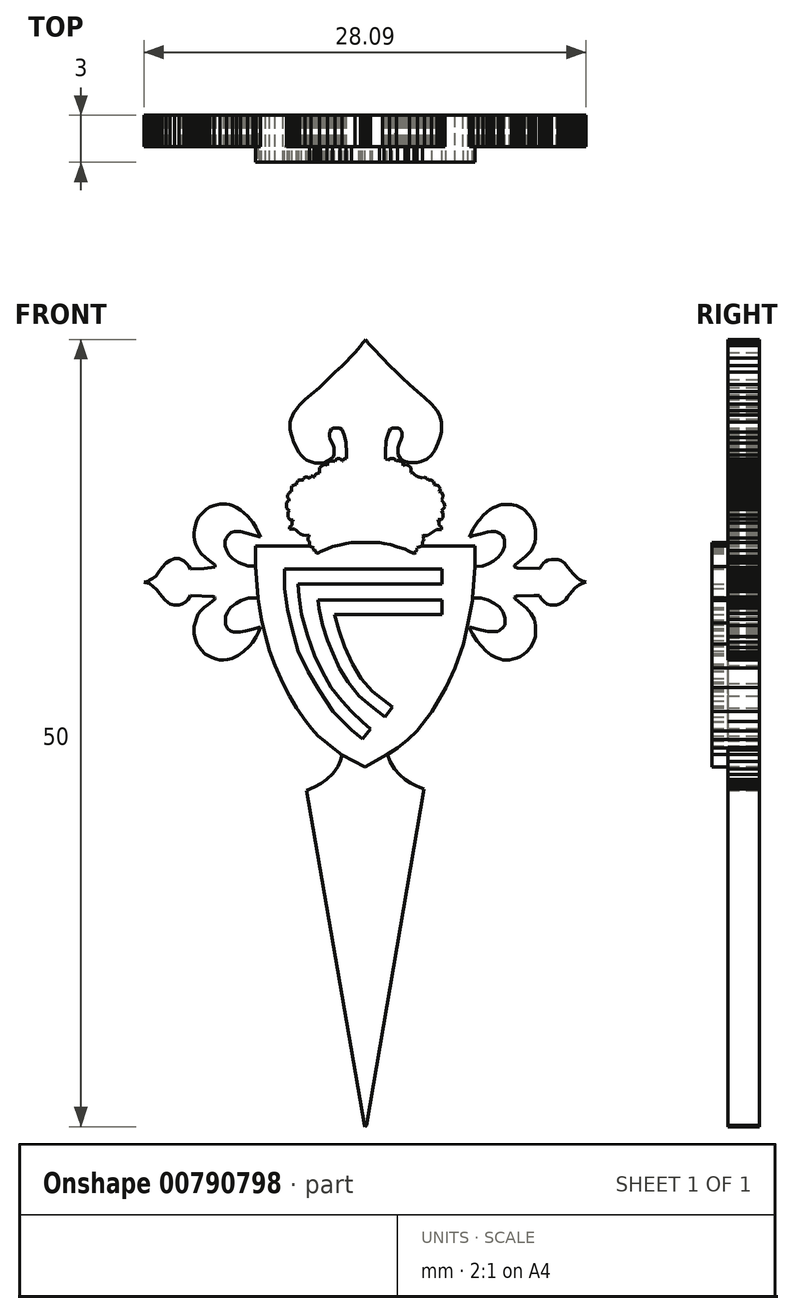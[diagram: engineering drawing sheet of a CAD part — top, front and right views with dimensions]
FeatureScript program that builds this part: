
annotation { "Feature Type Name" : "Feature", "Feature Type Description" : "" }
export const myFeature = defineFeature(function(context is Context, id is Id, definition is map)
    precondition{}
    {
        {
            var Q0;
            Q0=qCreatedBy(makeId("Front.planeOp"),FACE);
            var sketch = newSketch(context, id + "F0", { "sketchPlane" : qUnion([Q0])});
            skLineSegment(sketch, "E0", {"start": v(14.06, 0) * mm, "end": v(10.39, 21.27) * mm});
            skPoint(sketch, "E0.startSnap0", {"position": v(14.06, -0.08) * mm});
            skLineSegment(sketch, "E1", {"start": v(10.39, 21.27) * mm, "end": v(10.9, 21.5) * mm});
            skLineSegment(sketch, "E2", {"start": v(10.9, 21.5) * mm, "end": v(11.32, 21.71) * mm});
            skLineSegment(sketch, "E3", {"start": v(11.32, 21.71) * mm, "end": v(11.67, 21.99) * mm});
            skLineSegment(sketch, "E4", {"start": v(11.67, 21.99) * mm, "end": v(12.06, 22.35) * mm});
            skLineSegment(sketch, "E5", {"start": v(12.06, 22.35) * mm, "end": v(12.39, 22.8) * mm});
            skLineSegment(sketch, "E6", {"start": v(12.39, 22.8) * mm, "end": v(12.57, 23.17) * mm});
            skLineSegment(sketch, "E7", {"start": v(12.57, 23.17) * mm, "end": v(12.65, 23.55) * mm});
            skLineSegment(sketch, "E8", {"start": v(12.65, 23.55) * mm, "end": v(11.92, 24.1) * mm});
            skLineSegment(sketch, "E9", {"start": v(11.92, 24.1) * mm, "end": v(11.54, 24.4) * mm});
            skLineSegment(sketch, "E10", {"start": v(11.54, 24.4) * mm, "end": v(11.15, 24.74) * mm});
            skLineSegment(sketch, "E11", {"start": v(11.15, 24.74) * mm, "end": v(10.71, 25.21) * mm});
            skLineSegment(sketch, "E12", {"start": v(10.71, 25.21) * mm, "end": v(10.37, 25.64) * mm});
            skLineSegment(sketch, "E13", {"start": v(10.37, 25.64) * mm, "end": v(9.75, 26.5) * mm});
            skLineSegment(sketch, "E14", {"start": v(9.75, 26.5) * mm, "end": v(9.3, 27.27) * mm});
            skLineSegment(sketch, "E15", {"start": v(9.3, 27.27) * mm, "end": v(8.9, 28.06) * mm});
            skLineSegment(sketch, "E16", {"start": v(8.9, 28.06) * mm, "end": v(8.4, 29.21) * mm});
            skLineSegment(sketch, "E17", {"start": v(8.4, 29.21) * mm, "end": v(8.05, 30.15) * mm});
            skLineSegment(sketch, "E18", {"start": v(8.05, 30.15) * mm, "end": v(7.79, 31.09) * mm});
            skLineSegment(sketch, "E19", {"start": v(7.79, 31.09) * mm, "end": v(7.54, 32.09) * mm});
            skLineSegment(sketch, "E20", {"start": v(7.54, 32.09) * mm, "end": v(7.4, 32.9) * mm});
            skLineSegment(sketch, "E21", {"start": v(7.4, 32.9) * mm, "end": v(7.32, 33.46) * mm});
            skLineSegment(sketch, "E22", {"start": v(7.32, 33.46) * mm, "end": v(7.32, 33.5) * mm});
            skLineSegment(sketch, "E23", {"start": v(6.97, 33.5) * mm, "end": v(6.72, 33.5) * mm});
            skLineSegment(sketch, "E24", {"start": v(6.72, 33.5) * mm, "end": v(6.45, 33.4) * mm});
            skLineSegment(sketch, "E25", {"start": v(6.45, 33.4) * mm, "end": v(6.24, 33.33) * mm});
            skLineSegment(sketch, "E26", {"start": v(6.24, 33.33) * mm, "end": v(5.92, 33.16) * mm});
            skLineSegment(sketch, "E27", {"start": v(5.92, 33.16) * mm, "end": v(5.56, 32.88) * mm});
            skLineSegment(sketch, "E28", {"start": v(5.56, 32.88) * mm, "end": v(5.37, 32.61) * mm});
            skLineSegment(sketch, "E29", {"start": v(5.37, 32.61) * mm, "end": v(5.26, 32.32) * mm});
            skLineSegment(sketch, "E30", {"start": v(5.26, 32.32) * mm, "end": v(5.26, 31.8) * mm});
            skLineSegment(sketch, "E31", {"start": v(5.26, 31.8) * mm, "end": v(5.39, 31.56) * mm});
            skLineSegment(sketch, "E32", {"start": v(5.39, 31.56) * mm, "end": v(5.58, 31.4) * mm});
            skLineSegment(sketch, "E33", {"start": v(5.58, 31.4) * mm, "end": v(5.77, 31.33) * mm});
            skLineSegment(sketch, "E34", {"start": v(5.77, 31.33) * mm, "end": v(6.17, 31.33) * mm});
            skLineSegment(sketch, "E35", {"start": v(6.17, 31.33) * mm, "end": v(6.53, 31.4) * mm});
            skLineSegment(sketch, "E36", {"start": v(6.53, 31.4) * mm, "end": v(6.9, 31.49) * mm});
            skLineSegment(sketch, "E37", {"start": v(6.9, 31.49) * mm, "end": v(7.47, 31.64) * mm});
            skLineSegment(sketch, "E38", {"start": v(7.47, 31.64) * mm, "end": v(7.36, 31.33) * mm});
            skLineSegment(sketch, "E39", {"start": v(7.36, 31.33) * mm, "end": v(7.18, 31.03) * mm});
            skLineSegment(sketch, "E40", {"start": v(7.18, 31.03) * mm, "end": v(6.97, 30.68) * mm});
            skLineSegment(sketch, "E41", {"start": v(6.97, 30.68) * mm, "end": v(6.76, 30.46) * mm});
            skLineSegment(sketch, "E42", {"start": v(6.76, 30.46) * mm, "end": v(6.38, 30.1) * mm});
            skLineSegment(sketch, "E43", {"start": v(6.38, 30.1) * mm, "end": v(6.03, 29.84) * mm});
            skLineSegment(sketch, "E44", {"start": v(6.03, 29.84) * mm, "end": v(5.67, 29.65) * mm});
            skLineSegment(sketch, "E45", {"start": v(5.67, 29.65) * mm, "end": v(5.37, 29.6) * mm});
            skLineSegment(sketch, "E46", {"start": v(5.37, 29.6) * mm, "end": v(5.12, 29.56) * mm});
            skLineSegment(sketch, "E47", {"start": v(5.12, 29.56) * mm, "end": v(4.88, 29.56) * mm});
            skLineSegment(sketch, "E48", {"start": v(4.88, 29.56) * mm, "end": v(4.65, 29.63) * mm});
            skLineSegment(sketch, "E49", {"start": v(4.65, 29.63) * mm, "end": v(4.4, 29.72) * mm});
            skLineSegment(sketch, "E50", {"start": v(4.4, 29.72) * mm, "end": v(3.96, 29.96) * mm});
            skLineSegment(sketch, "E51", {"start": v(3.96, 29.96) * mm, "end": v(3.7, 30.22) * mm});
            skLineSegment(sketch, "E52", {"start": v(3.7, 30.22) * mm, "end": v(3.45, 30.57) * mm});
            skLineSegment(sketch, "E53", {"start": v(3.45, 30.57) * mm, "end": v(3.3, 30.96) * mm});
            skLineSegment(sketch, "E54", {"start": v(3.3, 30.96) * mm, "end": v(3.24, 31.25) * mm});
            skLineSegment(sketch, "E55", {"start": v(3.24, 31.25) * mm, "end": v(3.24, 31.7) * mm});
            skLineSegment(sketch, "E56", {"start": v(3.51, 32.48) * mm, "end": v(3.7, 32.7) * mm});
            skLineSegment(sketch, "E57", {"start": v(3.7, 32.7) * mm, "end": v(3.89, 32.89) * mm});
            skLineSegment(sketch, "E58", {"start": v(3.89, 32.89) * mm, "end": v(4.12, 33.07) * mm});
            skLineSegment(sketch, "E59", {"start": v(4.12, 33.07) * mm, "end": v(4.55, 33.4) * mm});
            skLineSegment(sketch, "E60", {"start": v(4.55, 33.4) * mm, "end": v(4.58, 33.5) * mm});
            skLineSegment(sketch, "E61", {"start": v(4.58, 33.5) * mm, "end": v(4.55, 33.57) * mm});
            skLineSegment(sketch, "E62", {"start": v(4.55, 33.57) * mm, "end": v(4.45, 33.6) * mm});
            skLineSegment(sketch, "E63", {"start": v(4.45, 33.6) * mm, "end": v(3.02, 33.66) * mm});
            skLineSegment(sketch, "E64", {"start": v(3.02, 33.66) * mm, "end": v(2.88, 33.4) * mm});
            skLineSegment(sketch, "E65", {"start": v(2.88, 33.4) * mm, "end": v(2.7, 33.25) * mm});
            skLineSegment(sketch, "E66", {"start": v(2.7, 33.25) * mm, "end": v(2.47, 33.13) * mm});
            skLineSegment(sketch, "E67", {"start": v(2.47, 33.13) * mm, "end": v(2.3, 33.07) * mm});
            skLineSegment(sketch, "E68", {"start": v(2.3, 33.07) * mm, "end": v(1.97, 33.07) * mm});
            skLineSegment(sketch, "E69", {"start": v(1.97, 33.07) * mm, "end": v(1.73, 33.12) * mm});
            skLineSegment(sketch, "E70", {"start": v(1.73, 33.12) * mm, "end": v(1.59, 33.23) * mm});
            skLineSegment(sketch, "E71", {"start": v(1.59, 33.23) * mm, "end": v(1.39, 33.4) * mm});
            skLineSegment(sketch, "E72", {"start": v(1.39, 33.4) * mm, "end": v(1.1, 33.76) * mm});
            skLineSegment(sketch, "E73", {"start": v(1.1, 33.76) * mm, "end": v(0.87, 34.05) * mm});
            skLineSegment(sketch, "E74", {"start": v(0.87, 34.05) * mm, "end": v(0.66, 34.23) * mm});
            skLineSegment(sketch, "E75", {"start": v(0.66, 34.23) * mm, "end": v(0.41, 34.4) * mm});
            skLineSegment(sketch, "E76", {"start": v(0.41, 34.4) * mm, "end": v(0.14, 34.49) * mm});
            skLineSegment(sketch, "E77", {"start": v(0.14, 34.49) * mm, "end": v(0.06, 34.5) * mm});
            skLineSegment(sketch, "E78", {"start": v(0.06, 34.5) * mm, "end": v(0.14, 34.52) * mm});
            skLineSegment(sketch, "E79", {"start": v(0.14, 34.52) * mm, "end": v(0.25, 34.55) * mm});
            skLineSegment(sketch, "E80", {"start": v(0.25, 34.55) * mm, "end": v(0.35, 34.59) * mm});
            skLineSegment(sketch, "E81", {"start": v(0.35, 34.59) * mm, "end": v(0.43, 34.64) * mm});
            skLineSegment(sketch, "E82", {"start": v(0.43, 34.64) * mm, "end": v(0.62, 34.74) * mm});
            skLineSegment(sketch, "E83", {"start": v(0.62, 34.74) * mm, "end": v(0.82, 34.91) * mm});
            skLineSegment(sketch, "E84", {"start": v(0.82, 34.91) * mm, "end": v(1.02, 35.17) * mm});
            skLineSegment(sketch, "E85", {"start": v(1.02, 35.17) * mm, "end": v(1.22, 35.44) * mm});
            skLineSegment(sketch, "E86", {"start": v(1.22, 35.44) * mm, "end": v(1.46, 35.7) * mm});
            skLineSegment(sketch, "E87", {"start": v(1.46, 35.7) * mm, "end": v(1.72, 35.9) * mm});
            skLineSegment(sketch, "E88", {"start": v(1.72, 35.9) * mm, "end": v(2, 36) * mm});
            skLineSegment(sketch, "E89", {"start": v(2, 36) * mm, "end": v(2.3, 36) * mm});
            skLineSegment(sketch, "E90", {"start": v(2.3, 36) * mm, "end": v(2.6, 35.84) * mm});
            skLineSegment(sketch, "E91", {"start": v(2.6, 35.84) * mm, "end": v(2.8, 35.67) * mm});
            skLineSegment(sketch, "E92", {"start": v(2.8, 35.67) * mm, "end": v(2.93, 35.5) * mm});
            skLineSegment(sketch, "E93", {"start": v(2.93, 35.5) * mm, "end": v(3.02, 35.35) * mm});
            skLineSegment(sketch, "E94", {"start": v(3.02, 35.35) * mm, "end": v(3.89, 35.39) * mm});
            skLineSegment(sketch, "E95", {"start": v(3.89, 35.39) * mm, "end": v(4.58, 35.46) * mm});
            skLineSegment(sketch, "E96", {"start": v(4.58, 35.46) * mm, "end": v(4.58, 35.56) * mm});
            skLineSegment(sketch, "E97", {"start": v(4.58, 35.56) * mm, "end": v(4.55, 35.62) * mm});
            skLineSegment(sketch, "E98", {"start": v(4.55, 35.62) * mm, "end": v(4.3, 35.8) * mm});
            skLineSegment(sketch, "E99", {"start": v(4.3, 35.8) * mm, "end": v(3.97, 36.09) * mm});
            skLineSegment(sketch, "E100", {"start": v(3.97, 36.09) * mm, "end": v(3.7, 36.33) * mm});
            skLineSegment(sketch, "E101", {"start": v(3.7, 36.33) * mm, "end": v(3.5, 36.6) * mm});
            skLineSegment(sketch, "E102", {"start": v(3.5, 36.6) * mm, "end": v(3.35, 36.91) * mm});
            skLineSegment(sketch, "E103", {"start": v(3.35, 36.91) * mm, "end": v(3.28, 37.17) * mm});
            skLineSegment(sketch, "E104", {"start": v(3.28, 37.17) * mm, "end": v(3.23, 37.4) * mm});
            skLineSegment(sketch, "E105", {"start": v(3.23, 37.4) * mm, "end": v(3.23, 37.58) * mm});
            skLineSegment(sketch, "E106", {"start": v(3.23, 37.58) * mm, "end": v(3.28, 37.88) * mm});
            skLineSegment(sketch, "E107", {"start": v(3.28, 37.88) * mm, "end": v(3.34, 38.12) * mm});
            skLineSegment(sketch, "E108", {"start": v(3.34, 38.12) * mm, "end": v(3.42, 38.4) * mm});
            skLineSegment(sketch, "E109", {"start": v(3.42, 38.4) * mm, "end": v(3.57, 38.67) * mm});
            skLineSegment(sketch, "E110", {"start": v(3.57, 38.67) * mm, "end": v(3.78, 38.9) * mm});
            skLineSegment(sketch, "E111", {"start": v(3.78, 38.9) * mm, "end": v(4.02, 39.12) * mm});
            skLineSegment(sketch, "E112", {"start": v(4.02, 39.12) * mm, "end": v(4.25, 39.27) * mm});
            skLineSegment(sketch, "E113", {"start": v(4.25, 39.27) * mm, "end": v(4.52, 39.38) * mm});
            skLineSegment(sketch, "E114", {"start": v(4.91, 39.48) * mm, "end": v(5.32, 39.48) * mm});
            skLineSegment(sketch, "E115", {"start": v(5.32, 39.48) * mm, "end": v(5.5, 39.43) * mm});
            skLineSegment(sketch, "E116", {"start": v(5.5, 39.43) * mm, "end": v(5.7, 39.36) * mm});
            skLineSegment(sketch, "E117", {"start": v(5.7, 39.36) * mm, "end": v(5.94, 39.25) * mm});
            skLineSegment(sketch, "E118", {"start": v(5.94, 39.25) * mm, "end": v(6.2, 39.1) * mm});
            skLineSegment(sketch, "E119", {"start": v(6.66, 38.7) * mm, "end": v(7, 38.3) * mm});
            skLineSegment(sketch, "E120", {"start": v(7, 38.3) * mm, "end": v(7.19, 37.98) * mm});
            skLineSegment(sketch, "E121", {"start": v(7.19, 37.98) * mm, "end": v(7.48, 37.38) * mm});
            skLineSegment(sketch, "E122", {"start": v(7.48, 37.38) * mm, "end": v(6.43, 37.67) * mm});
            skLineSegment(sketch, "E123", {"start": v(6.43, 37.67) * mm, "end": v(6.22, 37.73) * mm});
            skLineSegment(sketch, "E124", {"start": v(6.22, 37.73) * mm, "end": v(5.83, 37.73) * mm});
            skLineSegment(sketch, "E125", {"start": v(5.83, 37.73) * mm, "end": v(5.6, 37.67) * mm});
            skLineSegment(sketch, "E126", {"start": v(5.6, 37.67) * mm, "end": v(5.4, 37.48) * mm});
            skLineSegment(sketch, "E127", {"start": v(5.4, 37.48) * mm, "end": v(5.27, 37.27) * mm});
            skLineSegment(sketch, "E128", {"start": v(5.27, 37.27) * mm, "end": v(5.23, 37.12) * mm});
            skLineSegment(sketch, "E129", {"start": v(5.23, 37.12) * mm, "end": v(5.23, 36.8) * mm});
            skLineSegment(sketch, "E130", {"start": v(5.23, 36.8) * mm, "end": v(5.31, 36.55) * mm});
            skLineSegment(sketch, "E131", {"start": v(5.31, 36.55) * mm, "end": v(5.48, 36.23) * mm});
            skLineSegment(sketch, "E132", {"start": v(5.48, 36.23) * mm, "end": v(5.7, 36) * mm});
            skLineSegment(sketch, "E133", {"start": v(5.7, 36) * mm, "end": v(6.08, 35.75) * mm});
            skLineSegment(sketch, "E134", {"start": v(6.08, 35.75) * mm, "end": v(6.67, 35.52) * mm});
            skLineSegment(sketch, "E135", {"start": v(6.67, 35.52) * mm, "end": v(7.16, 35.52) * mm});
            skLineSegment(sketch, "E136", {"start": v(7.16, 35.52) * mm, "end": v(7.16, 36.8) * mm});
            skLineSegment(sketch, "E137", {"start": v(10.58, 36.8) * mm, "end": v(10.58, 37.07) * mm});
            skLineSegment(sketch, "E138", {"start": v(10.58, 37.07) * mm, "end": v(10.48, 37.16) * mm});
            skLineSegment(sketch, "E139", {"start": v(10.48, 37.16) * mm, "end": v(10.48, 37.34) * mm});
            skLineSegment(sketch, "E140", {"start": v(10.48, 37.34) * mm, "end": v(10.54, 37.4) * mm});
            skLineSegment(sketch, "E141", {"start": v(10.54, 37.4) * mm, "end": v(10.54, 37.5) * mm});
            skLineSegment(sketch, "E142", {"start": v(10.54, 37.5) * mm, "end": v(10.35, 37.47) * mm});
            skLineSegment(sketch, "E143", {"start": v(10.35, 37.47) * mm, "end": v(10.17, 37.49) * mm});
            skLineSegment(sketch, "E144", {"start": v(10.17, 37.49) * mm, "end": v(10.01, 37.57) * mm});
            skLineSegment(sketch, "E145", {"start": v(10.01, 37.57) * mm, "end": v(9.86, 37.7) * mm});
            skLineSegment(sketch, "E146", {"start": v(9.86, 37.7) * mm, "end": v(9.72, 37.8) * mm});
            skLineSegment(sketch, "E147", {"start": v(9.72, 37.8) * mm, "end": v(9.64, 37.87) * mm});
            skLineSegment(sketch, "E148", {"start": v(9.64, 37.87) * mm, "end": v(9.3, 37.87) * mm});
            skLineSegment(sketch, "E149", {"start": v(9.3, 37.87) * mm, "end": v(9.3, 38) * mm});
            skLineSegment(sketch, "E150", {"start": v(9.3, 38) * mm, "end": v(9.48, 38.14) * mm});
            skLineSegment(sketch, "E151", {"start": v(9.48, 38.14) * mm, "end": v(9.48, 38.37) * mm});
            skLineSegment(sketch, "E152", {"start": v(9.48, 38.37) * mm, "end": v(9.54, 38.4) * mm});
            skLineSegment(sketch, "E153", {"start": v(9.54, 38.4) * mm, "end": v(9.54, 38.45) * mm});
            skLineSegment(sketch, "E154", {"start": v(9.54, 38.45) * mm, "end": v(9.43, 38.45) * mm});
            skLineSegment(sketch, "E155", {"start": v(9.43, 38.45) * mm, "end": v(9.34, 38.5) * mm});
            skLineSegment(sketch, "E156", {"start": v(9.34, 38.5) * mm, "end": v(9.3, 38.53) * mm});
            skLineSegment(sketch, "E157", {"start": v(9.3, 38.53) * mm, "end": v(9.2, 38.65) * mm});
            skLineSegment(sketch, "E158", {"start": v(9.2, 38.65) * mm, "end": v(9.2, 38.92) * mm});
            skLineSegment(sketch, "E159", {"start": v(9.2, 38.92) * mm, "end": v(9.24, 38.98) * mm});
            skLineSegment(sketch, "E160", {"start": v(9.24, 38.98) * mm, "end": v(9.3, 39.05) * mm});
            skLineSegment(sketch, "E161", {"start": v(9.3, 39.05) * mm, "end": v(9.22, 39.11) * mm});
            skLineSegment(sketch, "E162", {"start": v(9.22, 39.11) * mm, "end": v(9.13, 39.2) * mm});
            skLineSegment(sketch, "E163", {"start": v(9.13, 39.2) * mm, "end": v(9.1, 39.26) * mm});
            skLineSegment(sketch, "E164", {"start": v(9.1, 39.26) * mm, "end": v(9.1, 39.52) * mm});
            skLineSegment(sketch, "E165", {"start": v(9.1, 39.52) * mm, "end": v(9.13, 39.58) * mm});
            skLineSegment(sketch, "E166", {"start": v(9.13, 39.58) * mm, "end": v(9.18, 39.62) * mm});
            skLineSegment(sketch, "E167", {"start": v(9.18, 39.62) * mm, "end": v(9.23, 39.66) * mm});
            skLineSegment(sketch, "E168", {"start": v(9.23, 39.66) * mm, "end": v(9.3, 39.66) * mm});
            skLineSegment(sketch, "E169", {"start": v(9.3, 39.66) * mm, "end": v(9.3, 39.74) * mm});
            skLineSegment(sketch, "E170", {"start": v(9.3, 39.74) * mm, "end": v(9.25, 39.8) * mm});
            skLineSegment(sketch, "E171", {"start": v(9.25, 39.8) * mm, "end": v(9.2, 39.87) * mm});
            skLineSegment(sketch, "E172", {"start": v(9.2, 39.87) * mm, "end": v(9.2, 40.03) * mm});
            skLineSegment(sketch, "E173", {"start": v(9.2, 40.03) * mm, "end": v(9.24, 40.1) * mm});
            skLineSegment(sketch, "E174", {"start": v(9.24, 40.1) * mm, "end": v(9.27, 40.16) * mm});
            skLineSegment(sketch, "E175", {"start": v(9.27, 40.16) * mm, "end": v(9.33, 40.2) * mm});
            skLineSegment(sketch, "E176", {"start": v(9.33, 40.2) * mm, "end": v(9.38, 40.25) * mm});
            skLineSegment(sketch, "E177", {"start": v(9.38, 40.25) * mm, "end": v(9.43, 40.26) * mm});
            skLineSegment(sketch, "E178", {"start": v(9.43, 40.26) * mm, "end": v(9.43, 40.5) * mm});
            skLineSegment(sketch, "E179", {"start": v(9.43, 40.5) * mm, "end": v(9.48, 40.6) * mm});
            skLineSegment(sketch, "E180", {"start": v(9.48, 40.6) * mm, "end": v(9.59, 40.66) * mm});
            skLineSegment(sketch, "E181", {"start": v(9.59, 40.66) * mm, "end": v(9.64, 40.7) * mm});
            skLineSegment(sketch, "E182", {"start": v(9.64, 40.7) * mm, "end": v(9.77, 40.7) * mm});
            skLineSegment(sketch, "E183", {"start": v(9.77, 40.7) * mm, "end": v(9.77, 40.85) * mm});
            skLineSegment(sketch, "E184", {"start": v(9.77, 40.85) * mm, "end": v(9.8, 40.9) * mm});
            skLineSegment(sketch, "E185", {"start": v(9.8, 40.9) * mm, "end": v(9.86, 40.95) * mm});
            skLineSegment(sketch, "E186", {"start": v(9.86, 40.95) * mm, "end": v(9.9, 41) * mm});
            skLineSegment(sketch, "E187", {"start": v(9.9, 41) * mm, "end": v(10.14, 41) * mm});
            skLineSegment(sketch, "E188", {"start": v(10.14, 41) * mm, "end": v(10.21, 41.03) * mm});
            skLineSegment(sketch, "E189", {"start": v(10.21, 41.03) * mm, "end": v(10.21, 41.1) * mm});
            skLineSegment(sketch, "E190", {"start": v(10.21, 41.1) * mm, "end": v(10.27, 41.14) * mm});
            skLineSegment(sketch, "E191", {"start": v(10.27, 41.14) * mm, "end": v(10.34, 41.17) * mm});
            skLineSegment(sketch, "E192", {"start": v(10.34, 41.17) * mm, "end": v(10.42, 41.17) * mm});
            skLineSegment(sketch, "E193", {"start": v(10.42, 41.17) * mm, "end": v(10.47, 41.16) * mm});
            skLineSegment(sketch, "E194", {"start": v(10.47, 41.16) * mm, "end": v(10.54, 41.12) * mm});
            skLineSegment(sketch, "E195", {"start": v(10.54, 41.12) * mm, "end": v(10.58, 41.1) * mm});
            skLineSegment(sketch, "E196", {"start": v(10.58, 41.1) * mm, "end": v(10.6, 41.16) * mm});
            skLineSegment(sketch, "E197", {"start": v(10.6, 41.16) * mm, "end": v(10.65, 41.2) * mm});
            skLineSegment(sketch, "E198", {"start": v(10.65, 41.2) * mm, "end": v(10.7, 41.24) * mm});
            skLineSegment(sketch, "E199", {"start": v(10.7, 41.24) * mm, "end": v(10.74, 41.24) * mm});
            skLineSegment(sketch, "E200", {"start": v(10.74, 41.24) * mm, "end": v(10.8, 41.22) * mm});
            skLineSegment(sketch, "E201", {"start": v(10.8, 41.22) * mm, "end": v(10.84, 41.18) * mm});
            skLineSegment(sketch, "E202", {"start": v(10.84, 41.18) * mm, "end": v(10.89, 41.17) * mm});
            skLineSegment(sketch, "E203", {"start": v(10.89, 41.17) * mm, "end": v(10.89, 41.23) * mm});
            skLineSegment(sketch, "E204", {"start": v(10.89, 41.23) * mm, "end": v(10.92, 41.29) * mm});
            skLineSegment(sketch, "E205", {"start": v(10.92, 41.29) * mm, "end": v(10.94, 41.33) * mm});
            skLineSegment(sketch, "E206", {"start": v(10.94, 41.33) * mm, "end": v(11, 41.38) * mm});
            skLineSegment(sketch, "E207", {"start": v(11, 41.38) * mm, "end": v(11.05, 41.42) * mm});
            skLineSegment(sketch, "E208", {"start": v(11.05, 41.42) * mm, "end": v(11.1, 41.44) * mm});
            skLineSegment(sketch, "E209", {"start": v(11.1, 41.44) * mm, "end": v(11.23, 41.44) * mm});
            skLineSegment(sketch, "E210", {"start": v(11.23, 41.77) * mm, "end": v(11.28, 41.82) * mm});
            skLineSegment(sketch, "E211", {"start": v(11.28, 41.82) * mm, "end": v(11.33, 41.87) * mm});
            skLineSegment(sketch, "E212", {"start": v(11.33, 41.87) * mm, "end": v(11.4, 41.92) * mm});
            skLineSegment(sketch, "E213", {"start": v(11.4, 41.92) * mm, "end": v(11.47, 41.97) * mm});
            skLineSegment(sketch, "E214", {"start": v(11.47, 41.97) * mm, "end": v(11.66, 41.97) * mm});
            skLineSegment(sketch, "E215", {"start": v(11.66, 41.97) * mm, "end": v(11.73, 41.91) * mm});
            skLineSegment(sketch, "E216", {"start": v(11.73, 41.91) * mm, "end": v(11.73, 42.08) * mm});
            skLineSegment(sketch, "E217", {"start": v(11.73, 42.08) * mm, "end": v(11.86, 42.2) * mm});
            skLineSegment(sketch, "E218", {"start": v(11.86, 42.2) * mm, "end": v(12, 42.2) * mm});
            skLineSegment(sketch, "E219", {"start": v(12, 42.2) * mm, "end": v(12.13, 42.21) * mm});
            skLineSegment(sketch, "E220", {"start": v(12.13, 42.21) * mm, "end": v(12.2, 42.15) * mm});
            skLineSegment(sketch, "E221", {"start": v(12.2, 42.15) * mm, "end": v(12.23, 42.24) * mm});
            skLineSegment(sketch, "E222", {"start": v(12.23, 42.24) * mm, "end": v(12.28, 42.31) * mm});
            skLineSegment(sketch, "E223", {"start": v(12.28, 42.31) * mm, "end": v(12.34, 42.36) * mm});
            skLineSegment(sketch, "E224", {"start": v(12.34, 42.36) * mm, "end": v(12.5, 42.36) * mm});
            skLineSegment(sketch, "E225", {"start": v(12.5, 42.36) * mm, "end": v(12.6, 42.3) * mm});
            skLineSegment(sketch, "E226", {"start": v(12.6, 42.3) * mm, "end": v(12.66, 42.27) * mm});
            skLineSegment(sketch, "E227", {"start": v(12.66, 42.27) * mm, "end": v(12.67, 42.2) * mm});
            skLineSegment(sketch, "E228", {"start": v(12.67, 42.2) * mm, "end": v(12.7, 42.2) * mm});
            skLineSegment(sketch, "E229", {"start": v(12.7, 42.2) * mm, "end": v(12.7, 42.26) * mm});
            skLineSegment(sketch, "E230", {"start": v(12.7, 42.26) * mm, "end": v(12.77, 42.32) * mm});
            skLineSegment(sketch, "E231", {"start": v(12.77, 42.32) * mm, "end": v(12.85, 42.36) * mm});
            skLineSegment(sketch, "E232", {"start": v(12.85, 42.36) * mm, "end": v(12.94, 42.36) * mm});
            skLineSegment(sketch, "E233", {"start": v(12.94, 42.36) * mm, "end": v(12.94, 42.68) * mm});
            skLineSegment(sketch, "E234", {"start": v(12.94, 42.68) * mm, "end": v(12.88, 43.4) * mm});
            skLineSegment(sketch, "E235", {"start": v(12.88, 43.4) * mm, "end": v(12.76, 43.89) * mm});
            skLineSegment(sketch, "E236", {"start": v(12.76, 43.89) * mm, "end": v(12.64, 44.2) * mm});
            skLineSegment(sketch, "E237", {"start": v(12.64, 44.2) * mm, "end": v(12.48, 44.3) * mm});
            skLineSegment(sketch, "E238", {"start": v(12.48, 44.3) * mm, "end": v(12.11, 44.3) * mm});
            skLineSegment(sketch, "E239", {"start": v(12.11, 44.3) * mm, "end": v(11.98, 44.23) * mm});
            skLineSegment(sketch, "E240", {"start": v(11.98, 44.23) * mm, "end": v(11.89, 44.08) * mm});
            skLineSegment(sketch, "E241", {"start": v(11.89, 44.08) * mm, "end": v(11.85, 43.94) * mm});
            skLineSegment(sketch, "E242", {"start": v(11.85, 43.94) * mm, "end": v(11.85, 43.79) * mm});
            skLineSegment(sketch, "E243", {"start": v(11.85, 43.79) * mm, "end": v(11.9, 43.59) * mm});
            skLineSegment(sketch, "E244", {"start": v(12.1, 43.2) * mm, "end": v(12.14, 43.02) * mm});
            skLineSegment(sketch, "E245", {"start": v(12.14, 43.02) * mm, "end": v(12.14, 42.66) * mm});
            skLineSegment(sketch, "E246", {"start": v(12.14, 42.66) * mm, "end": v(12.1, 42.48) * mm});
            skLineSegment(sketch, "E247", {"start": v(12.1, 42.48) * mm, "end": v(11.93, 42.31) * mm});
            skLineSegment(sketch, "E248", {"start": v(11.93, 42.31) * mm, "end": v(11.73, 42.21) * mm});
            skLineSegment(sketch, "E249", {"start": v(11.73, 42.21) * mm, "end": v(11.61, 42.15) * mm});
            skLineSegment(sketch, "E250", {"start": v(11.61, 42.15) * mm, "end": v(11.46, 42.08) * mm});
            skLineSegment(sketch, "E251", {"start": v(11.46, 42.08) * mm, "end": v(10.94, 42.08) * mm});
            skLineSegment(sketch, "E252", {"start": v(10.94, 42.08) * mm, "end": v(10.74, 42.14) * mm});
            skLineSegment(sketch, "E253", {"start": v(10.74, 42.14) * mm, "end": v(10.54, 42.2) * mm});
            skLineSegment(sketch, "E254", {"start": v(10.54, 42.2) * mm, "end": v(10.4, 42.27) * mm});
            skLineSegment(sketch, "E255", {"start": v(10.4, 42.27) * mm, "end": v(10.22, 42.4) * mm});
            skLineSegment(sketch, "E256", {"start": v(10.22, 42.4) * mm, "end": v(10.09, 42.55) * mm});
            skLineSegment(sketch, "E257", {"start": v(10.09, 42.55) * mm, "end": v(9.91, 42.73) * mm});
            skLineSegment(sketch, "E258", {"start": v(9.57, 43.41) * mm, "end": v(9.5, 43.65) * mm});
            skLineSegment(sketch, "E259", {"start": v(9.5, 43.65) * mm, "end": v(9.43, 43.84) * mm});
            skLineSegment(sketch, "E260", {"start": v(9.43, 43.84) * mm, "end": v(9.34, 44.2) * mm});
            skLineSegment(sketch, "E261", {"start": v(9.34, 44.2) * mm, "end": v(9.34, 44.68) * mm});
            skLineSegment(sketch, "E262", {"start": v(9.34, 44.68) * mm, "end": v(9.38, 44.77) * mm});
            skLineSegment(sketch, "E263", {"start": v(9.38, 44.77) * mm, "end": v(9.4, 44.86) * mm});
            skLineSegment(sketch, "E264", {"start": v(9.4, 44.86) * mm, "end": v(9.5, 45.1) * mm});
            skLineSegment(sketch, "E265", {"start": v(9.5, 45.1) * mm, "end": v(9.6, 45.3) * mm});
            skLineSegment(sketch, "E266", {"start": v(9.6, 45.3) * mm, "end": v(9.7, 45.4) * mm});
            skLineSegment(sketch, "E267", {"start": v(9.7, 45.4) * mm, "end": v(9.85, 45.62) * mm});
            skLineSegment(sketch, "E268", {"start": v(9.85, 45.62) * mm, "end": v(9.96, 45.76) * mm});
            skLineSegment(sketch, "E269", {"start": v(9.96, 45.76) * mm, "end": v(10.3, 46.1) * mm});
            skLineSegment(sketch, "E270", {"start": v(10.3, 46.1) * mm, "end": v(10.7, 46.41) * mm});
            skLineSegment(sketch, "E271", {"start": v(10.7, 46.41) * mm, "end": v(11.23, 46.87) * mm});
            skLineSegment(sketch, "E272", {"start": v(11.23, 46.87) * mm, "end": v(11.73, 47.36) * mm});
            skLineSegment(sketch, "E273", {"start": v(11.73, 47.36) * mm, "end": v(12.2, 47.85) * mm});
            skLineSegment(sketch, "E274", {"start": v(12.2, 47.85) * mm, "end": v(12.63, 48.23) * mm});
            skLineSegment(sketch, "E275", {"start": v(12.63, 48.23) * mm, "end": v(13.47, 49.09) * mm});
            skLineSegment(sketch, "E276", {"start": v(13.47, 49.09) * mm, "end": v(13.8, 49.5) * mm});
            skLineSegment(sketch, "E277", {"start": v(13.8, 49.5) * mm, "end": v(13.96, 49.68) * mm});
            skLineSegment(sketch, "E278", {"start": v(13.96, 49.68) * mm, "end": v(14.08, 49.83) * mm});
            skLineSegment(sketch, "E279", {"start": v(14.08, 49.83) * mm, "end": v(14.15, 49.92) * mm});
            skLineSegment(sketch, "E280", {"start": v(14.15, 49.92) * mm, "end": v(14.22, 49.81) * mm});
            skLineSegment(sketch, "E281", {"start": v(14.22, 49.81) * mm, "end": v(14.3, 49.7) * mm});
            skLineSegment(sketch, "E282", {"start": v(14.3, 49.7) * mm, "end": v(14.45, 49.53) * mm});
            skLineSegment(sketch, "E283", {"start": v(14.45, 49.53) * mm, "end": v(14.6, 49.37) * mm});
            skLineSegment(sketch, "E284", {"start": v(14.6, 49.37) * mm, "end": v(15.2, 48.73) * mm});
            skLineSegment(sketch, "E285", {"start": v(15.2, 48.73) * mm, "end": v(15.66, 48.26) * mm});
            skLineSegment(sketch, "E286", {"start": v(15.66, 48.26) * mm, "end": v(16.1, 47.84) * mm});
            skLineSegment(sketch, "E287", {"start": v(16.1, 47.84) * mm, "end": v(16.45, 47.5) * mm});
            skLineSegment(sketch, "E288", {"start": v(16.45, 47.5) * mm, "end": v(16.93, 47.06) * mm});
            skLineSegment(sketch, "E289", {"start": v(16.93, 47.06) * mm, "end": v(17.45, 46.62) * mm});
            skLineSegment(sketch, "E290", {"start": v(17.45, 46.62) * mm, "end": v(17.9, 46.23) * mm});
            skLineSegment(sketch, "E291", {"start": v(17.9, 46.23) * mm, "end": v(18.32, 45.81) * mm});
            skLineSegment(sketch, "E292", {"start": v(18.32, 45.81) * mm, "end": v(18.67, 45.4) * mm});
            skLineSegment(sketch, "E293", {"start": v(18.67, 45.4) * mm, "end": v(18.82, 45.12) * mm});
            skLineSegment(sketch, "E294", {"start": v(18.82, 45.12) * mm, "end": v(18.96, 44.69) * mm});
            skLineSegment(sketch, "E295", {"start": v(18.96, 44.69) * mm, "end": v(18.96, 44.04) * mm});
            skLineSegment(sketch, "E296", {"start": v(18.96, 44.04) * mm, "end": v(18.88, 43.7) * mm});
            skLineSegment(sketch, "E297", {"start": v(18.88, 43.7) * mm, "end": v(18.74, 43.33) * mm});
            skLineSegment(sketch, "E298", {"start": v(18.74, 43.33) * mm, "end": v(18.55, 42.9) * mm});
            skLineSegment(sketch, "E299", {"start": v(18.55, 42.9) * mm, "end": v(18.33, 42.6) * mm});
            skLineSegment(sketch, "E300", {"start": v(18.33, 42.6) * mm, "end": v(18.03, 42.33) * mm});
            skLineSegment(sketch, "E301", {"start": v(18.03, 42.33) * mm, "end": v(17.66, 42.15) * mm});
            skLineSegment(sketch, "E302", {"start": v(17.66, 42.15) * mm, "end": v(17.4, 42.09) * mm});
            skLineSegment(sketch, "E303", {"start": v(17.4, 42.09) * mm, "end": v(16.9, 42.09) * mm});
            skLineSegment(sketch, "E304", {"start": v(16.9, 42.09) * mm, "end": v(16.6, 42.2) * mm});
            skLineSegment(sketch, "E305", {"start": v(16.6, 42.2) * mm, "end": v(16.35, 42.37) * mm});
            skLineSegment(sketch, "E306", {"start": v(16.35, 42.37) * mm, "end": v(16.2, 42.63) * mm});
            skLineSegment(sketch, "E307", {"start": v(16.2, 42.63) * mm, "end": v(16.2, 43.07) * mm});
            skLineSegment(sketch, "E308", {"start": v(16.2, 43.07) * mm, "end": v(16.28, 43.35) * mm});
            skLineSegment(sketch, "E309", {"start": v(16.28, 43.35) * mm, "end": v(16.4, 43.55) * mm});
            skLineSegment(sketch, "E310", {"start": v(16.4, 43.55) * mm, "end": v(16.47, 43.75) * mm});
            skLineSegment(sketch, "E311", {"start": v(16.47, 43.75) * mm, "end": v(16.47, 44.01) * mm});
            skLineSegment(sketch, "E312", {"start": v(16.47, 44.01) * mm, "end": v(16.4, 44.14) * mm});
            skLineSegment(sketch, "E313", {"start": v(16.4, 44.14) * mm, "end": v(16.32, 44.24) * mm});
            skLineSegment(sketch, "E314", {"start": v(16.32, 44.24) * mm, "end": v(16.2, 44.3) * mm});
            skLineSegment(sketch, "E315", {"start": v(15.86, 44.3) * mm, "end": v(15.71, 44.24) * mm});
            skLineSegment(sketch, "E316", {"start": v(15.71, 44.24) * mm, "end": v(15.64, 44.08) * mm});
            skLineSegment(sketch, "E317", {"start": v(15.64, 44.08) * mm, "end": v(15.56, 43.9) * mm});
            skLineSegment(sketch, "E318", {"start": v(15.56, 43.9) * mm, "end": v(15.47, 43.59) * mm});
            skLineSegment(sketch, "E319", {"start": v(15.47, 43.59) * mm, "end": v(15.45, 43.43) * mm});
            skLineSegment(sketch, "E320", {"start": v(15.45, 43.43) * mm, "end": v(15.45, 43.23) * mm});
            skLineSegment(sketch, "E321", {"start": v(15.45, 43.23) * mm, "end": v(15.4, 43) * mm});
            skLineSegment(sketch, "E322", {"start": v(15.4, 42.32) * mm, "end": v(15.49, 42.32) * mm});
            skLineSegment(sketch, "E323", {"start": v(15.49, 42.32) * mm, "end": v(15.56, 42.28) * mm});
            skLineSegment(sketch, "E324", {"start": v(15.56, 42.28) * mm, "end": v(15.56, 42.23) * mm});
            skLineSegment(sketch, "E325", {"start": v(15.56, 42.23) * mm, "end": v(15.6, 42.27) * mm});
            skLineSegment(sketch, "E326", {"start": v(15.6, 42.27) * mm, "end": v(15.67, 42.32) * mm});
            skLineSegment(sketch, "E327", {"start": v(15.67, 42.32) * mm, "end": v(15.73, 42.36) * mm});
            skLineSegment(sketch, "E328", {"start": v(15.73, 42.36) * mm, "end": v(15.9, 42.36) * mm});
            skLineSegment(sketch, "E329", {"start": v(15.9, 42.36) * mm, "end": v(15.98, 42.31) * mm});
            skLineSegment(sketch, "E330", {"start": v(15.98, 42.31) * mm, "end": v(16.05, 42.26) * mm});
            skLineSegment(sketch, "E331", {"start": v(16.05, 42.26) * mm, "end": v(16.07, 42.2) * mm});
            skLineSegment(sketch, "E332", {"start": v(16.07, 42.2) * mm, "end": v(16.07, 42.18) * mm});
            skLineSegment(sketch, "E333", {"start": v(16.07, 42.18) * mm, "end": v(16.14, 42.22) * mm});
            skLineSegment(sketch, "E334", {"start": v(16.14, 42.22) * mm, "end": v(16.22, 42.23) * mm});
            skLineSegment(sketch, "E335", {"start": v(16.22, 42.23) * mm, "end": v(16.3, 42.2) * mm});
            skLineSegment(sketch, "E336", {"start": v(16.3, 42.2) * mm, "end": v(16.38, 42.2) * mm});
            skLineSegment(sketch, "E337", {"start": v(16.38, 42.2) * mm, "end": v(16.45, 42.16) * mm});
            skLineSegment(sketch, "E338", {"start": v(16.45, 42.16) * mm, "end": v(16.5, 42.09) * mm});
            skLineSegment(sketch, "E339", {"start": v(16.5, 42.09) * mm, "end": v(16.53, 42.04) * mm});
            skLineSegment(sketch, "E340", {"start": v(16.53, 42.04) * mm, "end": v(16.53, 41.91) * mm});
            skLineSegment(sketch, "E341", {"start": v(16.53, 41.91) * mm, "end": v(16.6, 41.94) * mm});
            skLineSegment(sketch, "E342", {"start": v(16.6, 41.94) * mm, "end": v(16.72, 41.98) * mm});
            skLineSegment(sketch, "E343", {"start": v(16.72, 41.98) * mm, "end": v(16.8, 41.95) * mm});
            skLineSegment(sketch, "E344", {"start": v(16.8, 41.95) * mm, "end": v(16.9, 41.9) * mm});
            skLineSegment(sketch, "E345", {"start": v(16.9, 41.9) * mm, "end": v(17, 41.81) * mm});
            skLineSegment(sketch, "E346", {"start": v(17, 41.81) * mm, "end": v(17.03, 41.7) * mm});
            skLineSegment(sketch, "E347", {"start": v(17.03, 41.7) * mm, "end": v(17.03, 41.45) * mm});
            skLineSegment(sketch, "E348", {"start": v(17.03, 41.45) * mm, "end": v(17.15, 41.43) * mm});
            skLineSegment(sketch, "E349", {"start": v(17.15, 41.43) * mm, "end": v(17.22, 41.38) * mm});
            skLineSegment(sketch, "E350", {"start": v(17.22, 41.38) * mm, "end": v(17.4, 41.2) * mm});
            skLineSegment(sketch, "E351", {"start": v(17.4, 41.2) * mm, "end": v(17.43, 41.22) * mm});
            skLineSegment(sketch, "E352", {"start": v(17.76, 41.12) * mm, "end": v(17.84, 41.17) * mm});
            skLineSegment(sketch, "E353", {"start": v(17.84, 41.17) * mm, "end": v(17.9, 41.15) * mm});
            skLineSegment(sketch, "E354", {"start": v(17.9, 41.15) * mm, "end": v(17.98, 41.13) * mm});
            skLineSegment(sketch, "E355", {"start": v(17.98, 41.13) * mm, "end": v(18.03, 41.1) * mm});
            skLineSegment(sketch, "E356", {"start": v(18.03, 41.1) * mm, "end": v(18.07, 41.07) * mm});
            skLineSegment(sketch, "E357", {"start": v(18.07, 41.07) * mm, "end": v(18.1, 41) * mm});
            skLineSegment(sketch, "E358", {"start": v(18.1, 41) * mm, "end": v(18.1, 40.96) * mm});
            skLineSegment(sketch, "E359", {"start": v(18.1, 40.96) * mm, "end": v(18.15, 41) * mm});
            skLineSegment(sketch, "E360", {"start": v(18.15, 41) * mm, "end": v(18.3, 41) * mm});
            skLineSegment(sketch, "E361", {"start": v(18.3, 41) * mm, "end": v(18.36, 40.97) * mm});
            skLineSegment(sketch, "E362", {"start": v(18.36, 40.97) * mm, "end": v(18.4, 40.93) * mm});
            skLineSegment(sketch, "E363", {"start": v(18.4, 40.93) * mm, "end": v(18.44, 40.89) * mm});
            skLineSegment(sketch, "E364", {"start": v(18.44, 40.89) * mm, "end": v(18.48, 40.83) * mm});
            skLineSegment(sketch, "E365", {"start": v(18.48, 40.83) * mm, "end": v(18.5, 40.7) * mm});
            skLineSegment(sketch, "E366", {"start": v(18.5, 40.7) * mm, "end": v(18.74, 40.63) * mm});
            skLineSegment(sketch, "E367", {"start": v(18.74, 40.63) * mm, "end": v(18.9, 40.46) * mm});
            skLineSegment(sketch, "E368", {"start": v(18.9, 40.46) * mm, "end": v(18.8, 40.28) * mm});
            skLineSegment(sketch, "E369", {"start": v(18.8, 40.28) * mm, "end": v(18.96, 40.22) * mm});
            skLineSegment(sketch, "E370", {"start": v(18.96, 40.22) * mm, "end": v(19.08, 40) * mm});
            skLineSegment(sketch, "E371", {"start": v(19.08, 40) * mm, "end": v(19.02, 39.83) * mm});
            skLineSegment(sketch, "E372", {"start": v(19.02, 39.83) * mm, "end": v(18.97, 39.7) * mm});
            skLineSegment(sketch, "E373", {"start": v(18.97, 39.7) * mm, "end": v(19.13, 39.53) * mm});
            skLineSegment(sketch, "E374", {"start": v(19.13, 39.53) * mm, "end": v(19.18, 39.32) * mm});
            skLineSegment(sketch, "E375", {"start": v(19.18, 39.32) * mm, "end": v(19.13, 39.2) * mm});
            skLineSegment(sketch, "E376", {"start": v(19.13, 39.2) * mm, "end": v(18.96, 39.06) * mm});
            skLineSegment(sketch, "E377", {"start": v(18.96, 39.06) * mm, "end": v(19.06, 38.88) * mm});
            skLineSegment(sketch, "E378", {"start": v(19.06, 38.88) * mm, "end": v(19.06, 38.61) * mm});
            skLineSegment(sketch, "E379", {"start": v(19.06, 38.61) * mm, "end": v(18.97, 38.5) * mm});
            skLineSegment(sketch, "E380", {"start": v(18.97, 38.5) * mm, "end": v(18.74, 38.5) * mm});
            skLineSegment(sketch, "E381", {"start": v(18.74, 38.5) * mm, "end": v(18.8, 38.3) * mm});
            skLineSegment(sketch, "E382", {"start": v(18.8, 38.3) * mm, "end": v(18.82, 38.14) * mm});
            skLineSegment(sketch, "E383", {"start": v(18.82, 38.14) * mm, "end": v(18.96, 38) * mm});
            skLineSegment(sketch, "E384", {"start": v(18.96, 38) * mm, "end": v(18.96, 37.86) * mm});
            skLineSegment(sketch, "E385", {"start": v(18.96, 37.86) * mm, "end": v(18.64, 37.86) * mm});
            skLineSegment(sketch, "E386", {"start": v(18.64, 37.86) * mm, "end": v(18.18, 37.52) * mm});
            skLineSegment(sketch, "E387", {"start": v(18.18, 37.52) * mm, "end": v(18.07, 37.48) * mm});
            skLineSegment(sketch, "E388", {"start": v(18.07, 37.48) * mm, "end": v(17.78, 37.48) * mm});
            skLineSegment(sketch, "E389", {"start": v(17.78, 37.48) * mm, "end": v(17.77, 37.43) * mm});
            skLineSegment(sketch, "E390", {"start": v(17.77, 37.43) * mm, "end": v(17.84, 37.35) * mm});
            skLineSegment(sketch, "E391", {"start": v(17.84, 37.35) * mm, "end": v(17.84, 37.28) * mm});
            skLineSegment(sketch, "E392", {"start": v(17.84, 37.28) * mm, "end": v(17.86, 37.24) * mm});
            skLineSegment(sketch, "E393", {"start": v(17.86, 37.24) * mm, "end": v(17.84, 37.16) * mm});
            skLineSegment(sketch, "E394", {"start": v(17.84, 37.16) * mm, "end": v(17.77, 37.1) * mm});
            skLineSegment(sketch, "E395", {"start": v(17.77, 37.1) * mm, "end": v(17.77, 36.79) * mm});
            skLineSegment(sketch, "E396", {"start": v(17.77, 36.79) * mm, "end": v(20.72, 36.79) * mm});
            skLineSegment(sketch, "E397", {"start": v(21.1, 36.79) * mm, "end": v(20.72, 36.79) * mm});
            skLineSegment(sketch, "E398", {"start": v(14.06, 0) * mm, "end": v(14.1, -0.08) * mm});
            skLineSegment(sketch, "E399", {"start": v(14.1, -0.08) * mm, "end": v(14.19, 0) * mm});
            skLineSegment(sketch, "E400", {"start": v(14.19, 0) * mm, "end": v(17.87, 21.36) * mm});
            skLineSegment(sketch, "E401", {"start": v(17.87, 21.36) * mm, "end": v(17.6, 21.46) * mm});
            skLineSegment(sketch, "E402", {"start": v(17.6, 21.46) * mm, "end": v(17.31, 21.6) * mm});
            skLineSegment(sketch, "E403", {"start": v(17.31, 21.6) * mm, "end": v(17, 21.74) * mm});
            skLineSegment(sketch, "E404", {"start": v(17, 21.74) * mm, "end": v(16.65, 21.99) * mm});
            skLineSegment(sketch, "E405", {"start": v(16.65, 21.99) * mm, "end": v(16.3, 22.3) * mm});
            skLineSegment(sketch, "E406", {"start": v(16.3, 22.3) * mm, "end": v(16, 22.64) * mm});
            skLineSegment(sketch, "E407", {"start": v(16, 22.64) * mm, "end": v(15.7, 23.1) * mm});
            skLineSegment(sketch, "E408", {"start": v(15.7, 23.1) * mm, "end": v(15.55, 23.56) * mm});
            skLineSegment(sketch, "E409", {"start": v(15.55, 23.56) * mm, "end": v(16.19, 24) * mm});
            skLineSegment(sketch, "E410", {"start": v(16.19, 24) * mm, "end": v(16.83, 24.5) * mm});
            skLineSegment(sketch, "E411", {"start": v(16.83, 24.5) * mm, "end": v(17.41, 25.06) * mm});
            skLineSegment(sketch, "E412", {"start": v(17.41, 25.06) * mm, "end": v(17.87, 25.65) * mm});
            skLineSegment(sketch, "E413", {"start": v(17.87, 25.65) * mm, "end": v(18.35, 26.29) * mm});
            skLineSegment(sketch, "E414", {"start": v(18.35, 26.29) * mm, "end": v(19.24, 27.82) * mm});
            skLineSegment(sketch, "E415", {"start": v(19.24, 27.82) * mm, "end": v(19.8, 29.06) * mm});
            skLineSegment(sketch, "E416", {"start": v(19.8, 29.06) * mm, "end": v(20.34, 30.6) * mm});
            skLineSegment(sketch, "E417", {"start": v(20.34, 30.6) * mm, "end": v(20.65, 31.92) * mm});
            skLineSegment(sketch, "E418", {"start": v(20.65, 31.92) * mm, "end": v(20.93, 33.35) * mm});
            skLineSegment(sketch, "E419", {"start": v(20.93, 33.35) * mm, "end": v(20.93, 33.5) * mm});
            skLineSegment(sketch, "E420", {"start": v(20.93, 33.5) * mm, "end": v(21.46, 33.5) * mm});
            skLineSegment(sketch, "E421", {"start": v(21.46, 33.5) * mm, "end": v(21.93, 33.37) * mm});
            skLineSegment(sketch, "E422", {"start": v(21.93, 33.37) * mm, "end": v(22.33, 33.17) * mm});
            skLineSegment(sketch, "E423", {"start": v(22.33, 33.17) * mm, "end": v(22.65, 32.93) * mm});
            skLineSegment(sketch, "E424", {"start": v(22.65, 32.93) * mm, "end": v(22.85, 32.6) * mm});
            skLineSegment(sketch, "E425", {"start": v(22.85, 32.6) * mm, "end": v(22.98, 32.23) * mm});
            skLineSegment(sketch, "E426", {"start": v(22.98, 32.23) * mm, "end": v(22.98, 31.78) * mm});
            skLineSegment(sketch, "E427", {"start": v(22.98, 31.78) * mm, "end": v(22.84, 31.59) * mm});
            skLineSegment(sketch, "E428", {"start": v(21.91, 31.36) * mm, "end": v(21.46, 31.46) * mm});
            skLineSegment(sketch, "E429", {"start": v(21.46, 31.46) * mm, "end": v(20.74, 31.65) * mm});
            skLineSegment(sketch, "E430", {"start": v(20.74, 31.65) * mm, "end": v(20.76, 31.57) * mm});
            skLineSegment(sketch, "E431", {"start": v(20.76, 31.57) * mm, "end": v(20.8, 31.47) * mm});
            skLineSegment(sketch, "E432", {"start": v(20.8, 31.47) * mm, "end": v(20.93, 31.22) * mm});
            skLineSegment(sketch, "E433", {"start": v(20.93, 31.22) * mm, "end": v(21.2, 30.78) * mm});
            skLineSegment(sketch, "E434", {"start": v(21.2, 30.78) * mm, "end": v(21.78, 30.12) * mm});
            skLineSegment(sketch, "E435", {"start": v(21.78, 30.12) * mm, "end": v(22.1, 29.88) * mm});
            skLineSegment(sketch, "E436", {"start": v(22.1, 29.88) * mm, "end": v(22.42, 29.71) * mm});
            skLineSegment(sketch, "E437", {"start": v(22.42, 29.71) * mm, "end": v(22.7, 29.61) * mm});
            skLineSegment(sketch, "E438", {"start": v(22.7, 29.61) * mm, "end": v(22.87, 29.56) * mm});
            skLineSegment(sketch, "E439", {"start": v(22.87, 29.56) * mm, "end": v(23.27, 29.56) * mm});
            skLineSegment(sketch, "E440", {"start": v(23.27, 29.56) * mm, "end": v(23.5, 29.61) * mm});
            skLineSegment(sketch, "E441", {"start": v(23.5, 29.61) * mm, "end": v(23.76, 29.68) * mm});
            skLineSegment(sketch, "E442", {"start": v(23.76, 29.68) * mm, "end": v(23.99, 29.8) * mm});
            skLineSegment(sketch, "E443", {"start": v(23.99, 29.8) * mm, "end": v(24.22, 29.95) * mm});
            skLineSegment(sketch, "E444", {"start": v(24.22, 29.95) * mm, "end": v(24.35, 30.06) * mm});
            skLineSegment(sketch, "E445", {"start": v(24.35, 30.06) * mm, "end": v(24.61, 30.35) * mm});
            skLineSegment(sketch, "E446", {"start": v(24.61, 30.35) * mm, "end": v(24.8, 30.7) * mm});
            skLineSegment(sketch, "E447", {"start": v(24.8, 30.7) * mm, "end": v(24.95, 31.07) * mm});
            skLineSegment(sketch, "E448", {"start": v(24.95, 31.07) * mm, "end": v(24.95, 31.76) * mm});
            skLineSegment(sketch, "E449", {"start": v(24.95, 31.76) * mm, "end": v(24.85, 32.14) * mm});
            skLineSegment(sketch, "E450", {"start": v(24.85, 32.14) * mm, "end": v(24.65, 32.52) * mm});
            skLineSegment(sketch, "E451", {"start": v(24.65, 32.52) * mm, "end": v(24.37, 32.86) * mm});
            skLineSegment(sketch, "E452", {"start": v(24.37, 32.86) * mm, "end": v(24.04, 33.13) * mm});
            skLineSegment(sketch, "E453", {"start": v(24.04, 33.13) * mm, "end": v(23.66, 33.43) * mm});
            skLineSegment(sketch, "E454", {"start": v(23.66, 33.43) * mm, "end": v(23.62, 33.48) * mm});
            skLineSegment(sketch, "E455", {"start": v(23.62, 33.48) * mm, "end": v(23.61, 33.56) * mm});
            skLineSegment(sketch, "E456", {"start": v(23.61, 33.56) * mm, "end": v(23.68, 33.61) * mm});
            skLineSegment(sketch, "E457", {"start": v(23.68, 33.61) * mm, "end": v(23.78, 33.62) * mm});
            skLineSegment(sketch, "E458", {"start": v(23.78, 33.62) * mm, "end": v(24.84, 33.67) * mm});
            skLineSegment(sketch, "E459", {"start": v(24.84, 33.67) * mm, "end": v(25.2, 33.67) * mm});
            skLineSegment(sketch, "E460", {"start": v(25.2, 33.67) * mm, "end": v(25.3, 33.46) * mm});
            skLineSegment(sketch, "E461", {"start": v(25.3, 33.46) * mm, "end": v(25.47, 33.26) * mm});
            skLineSegment(sketch, "E462", {"start": v(25.47, 33.26) * mm, "end": v(25.67, 33.13) * mm});
            skLineSegment(sketch, "E463", {"start": v(25.67, 33.13) * mm, "end": v(25.88, 33.06) * mm});
            skLineSegment(sketch, "E464", {"start": v(25.88, 33.06) * mm, "end": v(26.28, 33.06) * mm});
            skLineSegment(sketch, "E465", {"start": v(26.28, 33.06) * mm, "end": v(26.45, 33.11) * mm});
            skLineSegment(sketch, "E466", {"start": v(26.45, 33.11) * mm, "end": v(26.67, 33.23) * mm});
            skLineSegment(sketch, "E467", {"start": v(26.67, 33.23) * mm, "end": v(26.86, 33.4) * mm});
            skLineSegment(sketch, "E468", {"start": v(26.86, 33.4) * mm, "end": v(26.96, 33.56) * mm});
            skLineSegment(sketch, "E469", {"start": v(26.96, 33.56) * mm, "end": v(27.26, 33.92) * mm});
            skLineSegment(sketch, "E470", {"start": v(27.26, 33.92) * mm, "end": v(27.45, 34.13) * mm});
            skLineSegment(sketch, "E471", {"start": v(27.45, 34.13) * mm, "end": v(27.7, 34.32) * mm});
            skLineSegment(sketch, "E472", {"start": v(27.7, 34.32) * mm, "end": v(27.88, 34.43) * mm});
            skLineSegment(sketch, "E473", {"start": v(27.88, 34.43) * mm, "end": v(28.15, 34.51) * mm});
            skLineSegment(sketch, "E474", {"start": v(28.15, 34.51) * mm, "end": v(28.05, 34.54) * mm});
            skLineSegment(sketch, "E475", {"start": v(28.05, 34.54) * mm, "end": v(27.91, 34.58) * mm});
            skLineSegment(sketch, "E476", {"start": v(27.91, 34.58) * mm, "end": v(27.85, 34.62) * mm});
            skLineSegment(sketch, "E477", {"start": v(27.85, 34.62) * mm, "end": v(27.73, 34.67) * mm});
            skLineSegment(sketch, "E478", {"start": v(27.73, 34.67) * mm, "end": v(27.6, 34.77) * mm});
            skLineSegment(sketch, "E479", {"start": v(27.6, 34.77) * mm, "end": v(27.45, 34.92) * mm});
            skLineSegment(sketch, "E480", {"start": v(27.45, 34.92) * mm, "end": v(27.3, 35.05) * mm});
            skLineSegment(sketch, "E481", {"start": v(27.3, 35.05) * mm, "end": v(27.15, 35.24) * mm});
            skLineSegment(sketch, "E482", {"start": v(27.15, 35.24) * mm, "end": v(26.98, 35.45) * mm});
            skLineSegment(sketch, "E483", {"start": v(26.98, 35.45) * mm, "end": v(26.76, 35.72) * mm});
            skLineSegment(sketch, "E484", {"start": v(26.76, 35.72) * mm, "end": v(26.55, 35.87) * mm});
            skLineSegment(sketch, "E485", {"start": v(26.55, 35.87) * mm, "end": v(26.38, 35.96) * mm});
            skLineSegment(sketch, "E486", {"start": v(26.38, 35.96) * mm, "end": v(25.94, 35.96) * mm});
            skLineSegment(sketch, "E487", {"start": v(25.94, 35.96) * mm, "end": v(25.73, 35.9) * mm});
            skLineSegment(sketch, "E488", {"start": v(25.73, 35.9) * mm, "end": v(25.58, 35.82) * mm});
            skLineSegment(sketch, "E489", {"start": v(25.58, 35.82) * mm, "end": v(25.44, 35.73) * mm});
            skLineSegment(sketch, "E490", {"start": v(25.44, 35.73) * mm, "end": v(25.34, 35.6) * mm});
            skLineSegment(sketch, "E491", {"start": v(25.34, 35.6) * mm, "end": v(25.22, 35.4) * mm});
            skLineSegment(sketch, "E492", {"start": v(25.22, 35.4) * mm, "end": v(25.2, 35.37) * mm});
            skLineSegment(sketch, "E493", {"start": v(25.2, 35.37) * mm, "end": v(23.8, 35.42) * mm});
            skLineSegment(sketch, "E494", {"start": v(23.8, 35.42) * mm, "end": v(23.64, 35.46) * mm});
            skLineSegment(sketch, "E495", {"start": v(23.64, 35.46) * mm, "end": v(23.6, 35.5) * mm});
            skLineSegment(sketch, "E496", {"start": v(23.6, 35.5) * mm, "end": v(23.6, 35.57) * mm});
            skLineSegment(sketch, "E497", {"start": v(23.6, 35.57) * mm, "end": v(23.65, 35.62) * mm});
            skLineSegment(sketch, "E498", {"start": v(23.65, 35.62) * mm, "end": v(24.3, 36.12) * mm});
            skLineSegment(sketch, "E499", {"start": v(24.3, 36.12) * mm, "end": v(24.69, 36.52) * mm});
            skLineSegment(sketch, "E500", {"start": v(24.69, 36.52) * mm, "end": v(24.89, 37) * mm});
            skLineSegment(sketch, "E501", {"start": v(24.89, 37) * mm, "end": v(24.95, 37.32) * mm});
            skLineSegment(sketch, "E502", {"start": v(24.95, 37.32) * mm, "end": v(24.95, 37.8) * mm});
            skLineSegment(sketch, "E503", {"start": v(24.95, 37.8) * mm, "end": v(24.85, 38.26) * mm});
            skLineSegment(sketch, "E504", {"start": v(24.85, 38.26) * mm, "end": v(24.71, 38.52) * mm});
            skLineSegment(sketch, "E505", {"start": v(24.71, 38.52) * mm, "end": v(24.54, 38.76) * mm});
            skLineSegment(sketch, "E506", {"start": v(24.54, 38.76) * mm, "end": v(24.2, 39.1) * mm});
            skLineSegment(sketch, "E507", {"start": v(24.2, 39.1) * mm, "end": v(24.1, 39.17) * mm});
            skLineSegment(sketch, "E508", {"start": v(24.1, 39.17) * mm, "end": v(23.9, 39.28) * mm});
            skLineSegment(sketch, "E509", {"start": v(23.9, 39.28) * mm, "end": v(23.74, 39.37) * mm});
            skLineSegment(sketch, "E510", {"start": v(23.74, 39.37) * mm, "end": v(23.54, 39.41) * mm});
            skLineSegment(sketch, "E511", {"start": v(23.54, 39.41) * mm, "end": v(23.41, 39.45) * mm});
            skLineSegment(sketch, "E512", {"start": v(23.41, 39.45) * mm, "end": v(22.87, 39.45) * mm});
            skLineSegment(sketch, "E513", {"start": v(22.87, 39.45) * mm, "end": v(22.76, 39.42) * mm});
            skLineSegment(sketch, "E514", {"start": v(22.76, 39.42) * mm, "end": v(22.58, 39.37) * mm});
            skLineSegment(sketch, "E515", {"start": v(22.58, 39.37) * mm, "end": v(22.46, 39.32) * mm});
            skLineSegment(sketch, "E516", {"start": v(22.46, 39.32) * mm, "end": v(22.26, 39.24) * mm});
            skLineSegment(sketch, "E517", {"start": v(22.26, 39.24) * mm, "end": v(22.05, 39.12) * mm});
            skLineSegment(sketch, "E518", {"start": v(22.05, 39.12) * mm, "end": v(21.85, 38.96) * mm});
            skLineSegment(sketch, "E519", {"start": v(21.85, 38.96) * mm, "end": v(21.61, 38.73) * mm});
            skLineSegment(sketch, "E520", {"start": v(21.61, 38.73) * mm, "end": v(21.42, 38.5) * mm});
            skLineSegment(sketch, "E521", {"start": v(21.42, 38.5) * mm, "end": v(21.3, 38.34) * mm});
            skLineSegment(sketch, "E522", {"start": v(21.3, 38.34) * mm, "end": v(20.96, 37.9) * mm});
            skLineSegment(sketch, "E523", {"start": v(20.96, 37.9) * mm, "end": v(20.75, 37.38) * mm});
            skLineSegment(sketch, "E524", {"start": v(20.75, 37.38) * mm, "end": v(21.01, 37.46) * mm});
            skLineSegment(sketch, "E525", {"start": v(21.01, 37.46) * mm, "end": v(21.46, 37.57) * mm});
            skLineSegment(sketch, "E526", {"start": v(21.46, 37.57) * mm, "end": v(21.88, 37.68) * mm});
            skLineSegment(sketch, "E527", {"start": v(21.88, 37.68) * mm, "end": v(22.1, 37.7) * mm});
            skLineSegment(sketch, "E528", {"start": v(22.1, 37.7) * mm, "end": v(22.4, 37.7) * mm});
            skLineSegment(sketch, "E529", {"start": v(22.4, 37.7) * mm, "end": v(22.48, 37.68) * mm});
            skLineSegment(sketch, "E530", {"start": v(22.48, 37.68) * mm, "end": v(22.55, 37.65) * mm});
            skLineSegment(sketch, "E531", {"start": v(22.55, 37.65) * mm, "end": v(22.67, 37.6) * mm});
            skLineSegment(sketch, "E532", {"start": v(22.67, 37.6) * mm, "end": v(22.82, 37.48) * mm});
            skLineSegment(sketch, "E533", {"start": v(22.82, 37.48) * mm, "end": v(22.95, 37.3) * mm});
            skLineSegment(sketch, "E534", {"start": v(22.95, 37.3) * mm, "end": v(22.98, 37.19) * mm});
            skLineSegment(sketch, "E535", {"start": v(22.98, 37.19) * mm, "end": v(22.98, 36.76) * mm});
            skLineSegment(sketch, "E536", {"start": v(22.98, 36.76) * mm, "end": v(22.87, 36.53) * mm});
            skLineSegment(sketch, "E537", {"start": v(22.87, 36.53) * mm, "end": v(22.8, 36.38) * mm});
            skLineSegment(sketch, "E538", {"start": v(22.8, 36.38) * mm, "end": v(22.68, 36.23) * mm});
            skLineSegment(sketch, "E539", {"start": v(22.68, 36.23) * mm, "end": v(22.6, 36.1) * mm});
            skLineSegment(sketch, "E540", {"start": v(22.6, 36.1) * mm, "end": v(22.26, 35.84) * mm});
            skLineSegment(sketch, "E541", {"start": v(22.26, 35.84) * mm, "end": v(21.97, 35.7) * mm});
            skLineSegment(sketch, "E542", {"start": v(21.97, 35.7) * mm, "end": v(21.61, 35.54) * mm});
            skLineSegment(sketch, "E543", {"start": v(21.61, 35.54) * mm, "end": v(21.54, 35.52) * mm});
            skLineSegment(sketch, "E544", {"start": v(21.54, 35.52) * mm, "end": v(21.1, 35.5) * mm});
            skLineSegment(sketch, "E545", {"start": v(3.24, 31.7) * mm, "end": v(3.51, 32.48) * mm});
            skLineSegment(sketch, "E546", {"start": v(7.32, 33.5) * mm, "end": v(6.97, 33.5) * mm});
            skLineSegment(sketch, "E547", {"start": v(4.52, 39.38) * mm, "end": v(4.91, 39.48) * mm});
            skLineSegment(sketch, "E548", {"start": v(6.2, 39.1) * mm, "end": v(6.66, 38.7) * mm});
            skLineSegment(sketch, "E549", {"start": v(7.16, 36.8) * mm, "end": v(10.58, 36.8) * mm});
            skLineSegment(sketch, "E550", {"start": v(11.23, 41.44) * mm, "end": v(11.23, 41.77) * mm});
            skLineSegment(sketch, "E551", {"start": v(11.9, 43.59) * mm, "end": v(12.1, 43.2) * mm});
            skLineSegment(sketch, "E552", {"start": v(9.91, 42.73) * mm, "end": v(9.57, 43.41) * mm});
            skLineSegment(sketch, "E553", {"start": v(15.4, 43) * mm, "end": v(15.4, 42.32) * mm});
            skLineSegment(sketch, "E554", {"start": v(15.86, 44.3) * mm, "end": v(16.2, 44.3) * mm});
            skLineSegment(sketch, "E555", {"start": v(17.43, 41.22) * mm, "end": v(17.76, 41.12) * mm});
            skLineSegment(sketch, "E556", {"start": v(22.84, 31.59) * mm, "end": v(22.57, 31.37) * mm});
            skLineSegment(sketch, "E557", {"start": v(22.57, 31.37) * mm, "end": v(21.91, 31.36) * mm});
            skLineSegment(sketch, "E558", {"start": v(21.1, 36.79) * mm, "end": v(21.1, 35.5) * mm});
            skSolve(sketch);
        }
        {
            var Q0;
            Q0=qCreatedBy(makeId("Front.planeOp"),FACE);
            var sketch = newSketch(context, id + "F1", { "sketchPlane" : qUnion([Q0])});
            skLineSegment(sketch, "E559", {"start": v(14.11, 22.77) * mm, "end": v(12.66, 23.54) * mm});
            skLineSegment(sketch, "E560", {"start": v(12.66, 23.54) * mm, "end": v(11.92, 24.1) * mm});
            skLineSegment(sketch, "E561", {"start": v(11.92, 24.1) * mm, "end": v(11.54, 24.41) * mm});
            skLineSegment(sketch, "E562", {"start": v(11.54, 24.41) * mm, "end": v(11.14, 24.75) * mm});
            skLineSegment(sketch, "E563", {"start": v(11.14, 24.75) * mm, "end": v(10.72, 25.2) * mm});
            skLineSegment(sketch, "E564", {"start": v(10.72, 25.2) * mm, "end": v(10.37, 25.65) * mm});
            skLineSegment(sketch, "E565", {"start": v(10.37, 25.65) * mm, "end": v(9.75, 26.5) * mm});
            skLineSegment(sketch, "E566", {"start": v(9.75, 26.5) * mm, "end": v(9.3, 27.27) * mm});
            skLineSegment(sketch, "E567", {"start": v(9.3, 27.27) * mm, "end": v(8.89, 28.06) * mm});
            skLineSegment(sketch, "E568", {"start": v(8.89, 28.06) * mm, "end": v(8.39, 29.21) * mm});
            skLineSegment(sketch, "E569", {"start": v(8.39, 29.21) * mm, "end": v(8.04, 30.15) * mm});
            skLineSegment(sketch, "E570", {"start": v(8.04, 30.15) * mm, "end": v(7.79, 31.09) * mm});
            skLineSegment(sketch, "E571", {"start": v(7.79, 31.09) * mm, "end": v(7.53, 32.1) * mm});
            skLineSegment(sketch, "E572", {"start": v(7.53, 32.1) * mm, "end": v(7.4, 32.9) * mm});
            skLineSegment(sketch, "E573", {"start": v(7.4, 32.9) * mm, "end": v(7.32, 33.46) * mm});
            skLineSegment(sketch, "E574", {"start": v(7.32, 33.46) * mm, "end": v(7.32, 33.5) * mm});
            skLineSegment(sketch, "E575", {"start": v(7.32, 33.5) * mm, "end": v(7.16, 35.51) * mm});
            skLineSegment(sketch, "E576", {"start": v(7.16, 35.51) * mm, "end": v(7.16, 36.8) * mm});
            skLineSegment(sketch, "E577", {"start": v(7.16, 36.8) * mm, "end": v(10.6, 36.8) * mm});
            skLineSegment(sketch, "E578", {"start": v(10.6, 36.8) * mm, "end": v(10.87, 36.67) * mm});
            skLineSegment(sketch, "E579", {"start": v(10.87, 36.67) * mm, "end": v(10.85, 36.63) * mm});
            skLineSegment(sketch, "E580", {"start": v(10.85, 36.63) * mm, "end": v(10.85, 36.55) * mm});
            skLineSegment(sketch, "E581", {"start": v(10.85, 36.55) * mm, "end": v(10.88, 36.53) * mm});
            skLineSegment(sketch, "E582", {"start": v(10.88, 36.53) * mm, "end": v(10.93, 36.54) * mm});
            skLineSegment(sketch, "E583", {"start": v(10.93, 36.54) * mm, "end": v(10.95, 36.53) * mm});
            skLineSegment(sketch, "E584", {"start": v(10.95, 36.53) * mm, "end": v(10.95, 36.44) * mm});
            skLineSegment(sketch, "E585", {"start": v(10.95, 36.44) * mm, "end": v(10.95, 36.4) * mm});
            skLineSegment(sketch, "E586", {"start": v(10.95, 36.4) * mm, "end": v(11.03, 36.35) * mm});
            skLineSegment(sketch, "E587", {"start": v(11.03, 36.35) * mm, "end": v(11.11, 36.35) * mm});
            skLineSegment(sketch, "E588", {"start": v(11.11, 36.35) * mm, "end": v(11.19, 36.4) * mm});
            skLineSegment(sketch, "E589", {"start": v(11.19, 36.4) * mm, "end": v(11.27, 36.45) * mm});
            skLineSegment(sketch, "E590", {"start": v(11.27, 36.45) * mm, "end": v(11.68, 36.62) * mm});
            skLineSegment(sketch, "E591", {"start": v(11.68, 36.62) * mm, "end": v(12.06, 36.75) * mm});
            skLineSegment(sketch, "E592", {"start": v(12.06, 36.75) * mm, "end": v(12.5, 36.88) * mm});
            skLineSegment(sketch, "E593", {"start": v(12.5, 36.88) * mm, "end": v(12.9, 36.97) * mm});
            skLineSegment(sketch, "E594", {"start": v(12.9, 36.97) * mm, "end": v(13.25, 37.01) * mm});
            skLineSegment(sketch, "E595", {"start": v(15.04, 37.01) * mm, "end": v(15.3, 36.96) * mm});
            skLineSegment(sketch, "E596", {"start": v(15.3, 36.96) * mm, "end": v(15.73, 36.9) * mm});
            skLineSegment(sketch, "E597", {"start": v(15.73, 36.9) * mm, "end": v(16.16, 36.75) * mm});
            skLineSegment(sketch, "E598", {"start": v(16.16, 36.75) * mm, "end": v(16.64, 36.6) * mm});
            skLineSegment(sketch, "E599", {"start": v(16.64, 36.6) * mm, "end": v(16.85, 36.5) * mm});
            skLineSegment(sketch, "E600", {"start": v(16.85, 36.5) * mm, "end": v(17.22, 36.33) * mm});
            skLineSegment(sketch, "E601", {"start": v(17.22, 36.33) * mm, "end": v(17.34, 36.39) * mm});
            skLineSegment(sketch, "E602", {"start": v(17.34, 36.39) * mm, "end": v(17.32, 36.54) * mm});
            skLineSegment(sketch, "E603", {"start": v(17.32, 36.54) * mm, "end": v(17.36, 36.55) * mm});
            skLineSegment(sketch, "E604", {"start": v(17.36, 36.55) * mm, "end": v(17.44, 36.62) * mm});
            skLineSegment(sketch, "E605", {"start": v(17.44, 36.62) * mm, "end": v(17.42, 36.7) * mm});
            skLineSegment(sketch, "E606", {"start": v(17.42, 36.7) * mm, "end": v(17.77, 36.79) * mm});
            skLineSegment(sketch, "E607", {"start": v(17.77, 36.79) * mm, "end": v(21.1, 36.79) * mm});
            skLineSegment(sketch, "E608", {"start": v(21.1, 36.79) * mm, "end": v(21.1, 35.5) * mm});
            skLineSegment(sketch, "E609", {"start": v(21.1, 35.5) * mm, "end": v(20.93, 33.5) * mm});
            skLineSegment(sketch, "E610", {"start": v(20.93, 33.5) * mm, "end": v(20.93, 33.35) * mm});
            skLineSegment(sketch, "E611", {"start": v(20.93, 33.35) * mm, "end": v(20.65, 31.92) * mm});
            skLineSegment(sketch, "E612", {"start": v(20.65, 31.92) * mm, "end": v(20.35, 30.59) * mm});
            skLineSegment(sketch, "E613", {"start": v(20.35, 30.59) * mm, "end": v(19.8, 29.06) * mm});
            skLineSegment(sketch, "E614", {"start": v(19.8, 29.06) * mm, "end": v(19.23, 27.8) * mm});
            skLineSegment(sketch, "E615", {"start": v(19.23, 27.8) * mm, "end": v(18.36, 26.3) * mm});
            skLineSegment(sketch, "E616", {"start": v(17.42, 25.07) * mm, "end": v(16.85, 24.53) * mm});
            skLineSegment(sketch, "E617", {"start": v(16.85, 24.53) * mm, "end": v(16.18, 23.99) * mm});
            skLineSegment(sketch, "E618", {"start": v(16.18, 23.99) * mm, "end": v(15.52, 23.56) * mm});
            skLineSegment(sketch, "E619", {"start": v(15.52, 23.56) * mm, "end": v(14.11, 22.77) * mm});
            skLineSegment(sketch, "E620", {"start": v(17.42, 25.07) * mm, "end": v(18.36, 26.3) * mm});
            skLineSegment(sketch, "E621", {"start": v(13.25, 37.01) * mm, "end": v(15.04, 37.01) * mm});
            skLineSegment(sketch, "E622", {"start": v(11.12, 33.36) * mm, "end": v(18.98, 33.36) * mm});
            skLineSegment(sketch, "E623", {"start": v(18.98, 32.46) * mm, "end": v(12.18, 32.46) * mm});
            skLineSegment(sketch, "E624", {"start": v(12.18, 32.46) * mm, "end": v(12.47, 31.43) * mm});
            skLineSegment(sketch, "E625", {"start": v(12.47, 31.43) * mm, "end": v(12.8, 30.4) * mm});
            skLineSegment(sketch, "E626", {"start": v(12.8, 30.4) * mm, "end": v(13.3, 29.31) * mm});
            skLineSegment(sketch, "E627", {"start": v(13.3, 29.31) * mm, "end": v(13.86, 28.39) * mm});
            skLineSegment(sketch, "E628", {"start": v(13.86, 28.39) * mm, "end": v(14.6, 27.58) * mm});
            skLineSegment(sketch, "E629", {"start": v(14.6, 27.58) * mm, "end": v(15.86, 26.57) * mm});
            skLineSegment(sketch, "E630", {"start": v(15.86, 26.57) * mm, "end": v(15.37, 25.94) * mm});
            skLineSegment(sketch, "E631", {"start": v(15.37, 25.94) * mm, "end": v(14.48, 26.64) * mm});
            skLineSegment(sketch, "E632", {"start": v(14.48, 26.64) * mm, "end": v(13.74, 27.3) * mm});
            skLineSegment(sketch, "E633", {"start": v(13.74, 27.3) * mm, "end": v(13.01, 28.18) * mm});
            skLineSegment(sketch, "E634", {"start": v(13.01, 28.18) * mm, "end": v(12.5, 29.03) * mm});
            skLineSegment(sketch, "E635", {"start": v(12.5, 29.03) * mm, "end": v(12.08, 29.97) * mm});
            skLineSegment(sketch, "E636", {"start": v(12.08, 29.97) * mm, "end": v(11.72, 30.82) * mm});
            skLineSegment(sketch, "E637", {"start": v(11.72, 30.82) * mm, "end": v(11.4, 31.79) * mm});
            skLineSegment(sketch, "E638", {"start": v(11.4, 31.79) * mm, "end": v(11.17, 32.83) * mm});
            skLineSegment(sketch, "E639", {"start": v(11.17, 32.83) * mm, "end": v(11.12, 33.36) * mm});
            skLineSegment(sketch, "E640", {"start": v(18.98, 33.36) * mm, "end": v(18.98, 32.46) * mm});
            skLineSegment(sketch, "E641", {"start": v(18.98, 35.35) * mm, "end": v(9, 35.35) * mm});
            skLineSegment(sketch, "E642", {"start": v(9, 35.35) * mm, "end": v(9, 34.1) * mm});
            skLineSegment(sketch, "E643", {"start": v(9, 34.1) * mm, "end": v(9.19, 32.78) * mm});
            skLineSegment(sketch, "E644", {"start": v(9.19, 32.78) * mm, "end": v(9.46, 31.56) * mm});
            skLineSegment(sketch, "E645", {"start": v(9.46, 31.56) * mm, "end": v(9.86, 30.15) * mm});
            skLineSegment(sketch, "E646", {"start": v(9.86, 30.15) * mm, "end": v(10.5, 28.84) * mm});
            skLineSegment(sketch, "E647", {"start": v(10.5, 28.84) * mm, "end": v(11.19, 27.64) * mm});
            skLineSegment(sketch, "E648", {"start": v(11.19, 27.64) * mm, "end": v(12.08, 26.3) * mm});
            skLineSegment(sketch, "E649", {"start": v(12.08, 26.3) * mm, "end": v(12.71, 25.65) * mm});
            skLineSegment(sketch, "E650", {"start": v(12.71, 25.65) * mm, "end": v(13.25, 25.12) * mm});
            skLineSegment(sketch, "E651", {"start": v(13.25, 25.12) * mm, "end": v(13.93, 24.55) * mm});
            skLineSegment(sketch, "E652", {"start": v(13.93, 24.55) * mm, "end": v(14.46, 25.19) * mm});
            skLineSegment(sketch, "E653", {"start": v(14.46, 25.19) * mm, "end": v(13.93, 25.63) * mm});
            skLineSegment(sketch, "E654", {"start": v(13.93, 25.63) * mm, "end": v(13.25, 26.3) * mm});
            skLineSegment(sketch, "E655", {"start": v(13.25, 26.3) * mm, "end": v(12.64, 26.96) * mm});
            skLineSegment(sketch, "E656", {"start": v(12.64, 26.96) * mm, "end": v(11.94, 27.83) * mm});
            skLineSegment(sketch, "E657", {"start": v(11.94, 27.83) * mm, "end": v(11.37, 28.87) * mm});
            skLineSegment(sketch, "E658", {"start": v(11.37, 28.87) * mm, "end": v(10.91, 29.85) * mm});
            skLineSegment(sketch, "E659", {"start": v(10.91, 29.85) * mm, "end": v(10.46, 31.1) * mm});
            skLineSegment(sketch, "E660", {"start": v(10.46, 31.1) * mm, "end": v(10.09, 32.46) * mm});
            skLineSegment(sketch, "E661", {"start": v(10.09, 32.46) * mm, "end": v(9.9, 33.6) * mm});
            skLineSegment(sketch, "E662", {"start": v(9.9, 33.6) * mm, "end": v(9.84, 34.37) * mm});
            skLineSegment(sketch, "E663", {"start": v(9.84, 34.37) * mm, "end": v(18.99, 34.37) * mm});
            skLineSegment(sketch, "E664", {"start": v(18.98, 35.35) * mm, "end": v(18.99, 34.37) * mm});
            skSolve(sketch);
        }
        {
            var Q0;
            Q0 = qSketchRegion(id + "F0", true);
            extrude(context, id + "F2", {"entities" : qUnion([Q0]), "depth" : 2 * mm, "offsetDistance" : 25 * mm});
        }
        {
            var Q0;
            Q0 = qSketchRegion(id + "F1", true);
            extrude(context, id + "F3", {"entities" : qUnion([Q0]), "operationType" : NewBodyOperationType.ADD, "depth" : 3 * mm, "offsetDistance" : 25 * mm});
        }
    });
